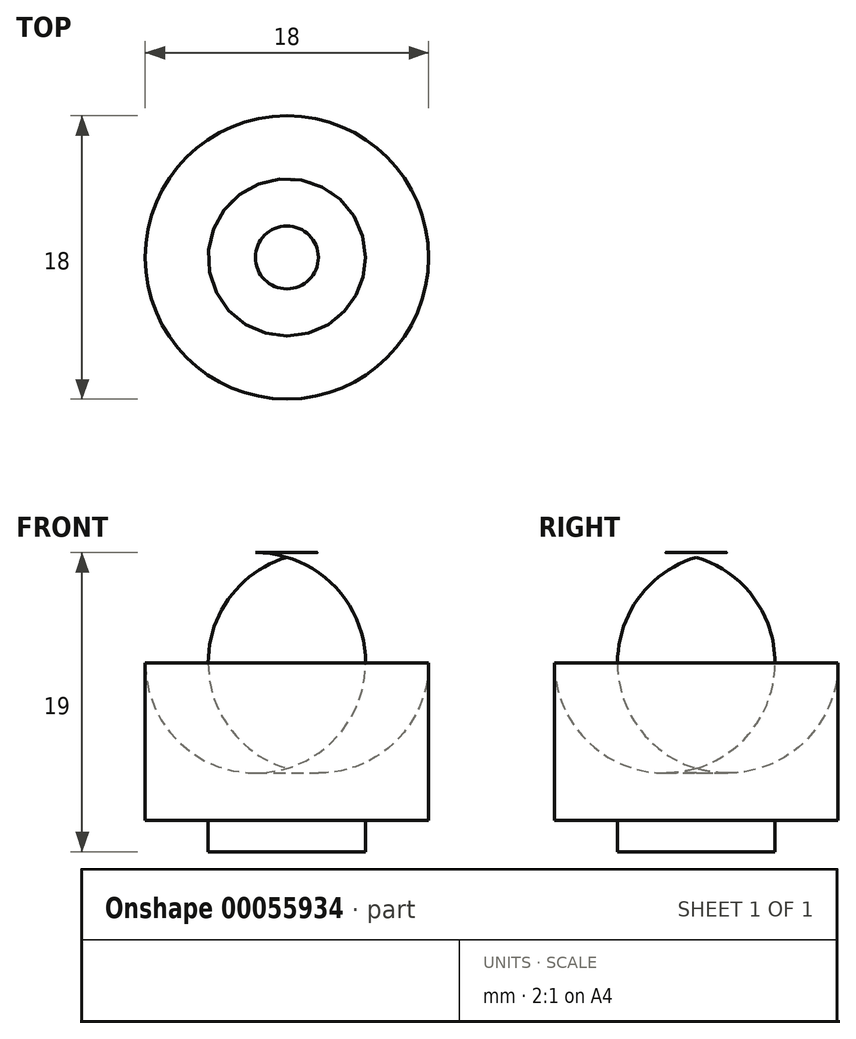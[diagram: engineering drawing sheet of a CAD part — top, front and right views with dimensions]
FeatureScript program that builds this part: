
annotation { "Feature Type Name" : "Feature", "Feature Type Description" : "" }
export const myFeature = defineFeature(function(context is Context, id is Id, definition is map)
    precondition{}
    {
        {
            var Q0;
            Q0=qCreatedBy(makeId("Front.planeOp"),FACE);
            var sketch = newSketch(context, id + "F0", { "sketchPlane" : qUnion([Q0])});
            skLineSegment(sketch, "E0", {"start": v(5, 0) * mm, "end": v(5, 2) * mm, "construction": true});
            skLineSegment(sketch, "E1", {"start": v(5, 2) * mm, "end": v(7.5, 2) * mm, "construction": true});
            skLineSegment(sketch, "E2", {"start": v(0, 19) * mm, "end": v(0, 0) * mm, "construction": true});
            skLineSegment(sketch, "E3", {"start": v(0, 0) * mm, "end": v(-5, 0) * mm});
            skLineSegment(sketch, "E4", {"start": v(-5, 0) * mm, "end": v(-5, 2) * mm});
            skLineSegment(sketch, "E5", {"start": v(-5, 2) * mm, "end": v(-9, 2) * mm});
            skLineSegment(sketch, "E6", {"start": v(-9, 2) * mm, "end": v(-9, 19) * mm});
            skLineSegment(sketch, "E7", {"start": v(-9, 19) * mm, "end": v(0, 19) * mm});
            skLineSegment(sketch, "E8", {"start": v(0, 19) * mm, "end": v(0, 0) * mm});
            skSolve(sketch);
        }
        {
            var Q0;
            Q0=makeQuery(id+"F0.imprint","IMPRINT",FACE,{"disambiguationData":[TD([[makeQuery(id+"F0.imprint","IMPRINT",EDGE,{"derivedFrom":sQuery(id+"F0.wireOp",EDGE,"E3")}),-1.0]])]});
            var Q1;
            Q1=sQuery(id+"F0.wireOp",EDGE,"E8");
            revolve(context, id + "F1", {"entities" : qUnion([Q0]), "axis" : qUnion([Q1]), "revolveType" : RevolveType.FULL});
        }
        {
            var Q0;
            Q0=makeQuery(id+"F1.opRevolve","SWEPT_EDGE",EDGE,{"disambiguationData":[OSD([sQuery(id+"F0.wireOp",EDGE,"E6"),sQuery(id+"F0.wireOp",EDGE,"E7")])]});
            fillet(context, id + "F2", {"entities" : qUnion([Q0]), "radius" : 7 * mm, "tangentPropagation" : true, "allowEdgeOverflow" : false});
        }
    });
